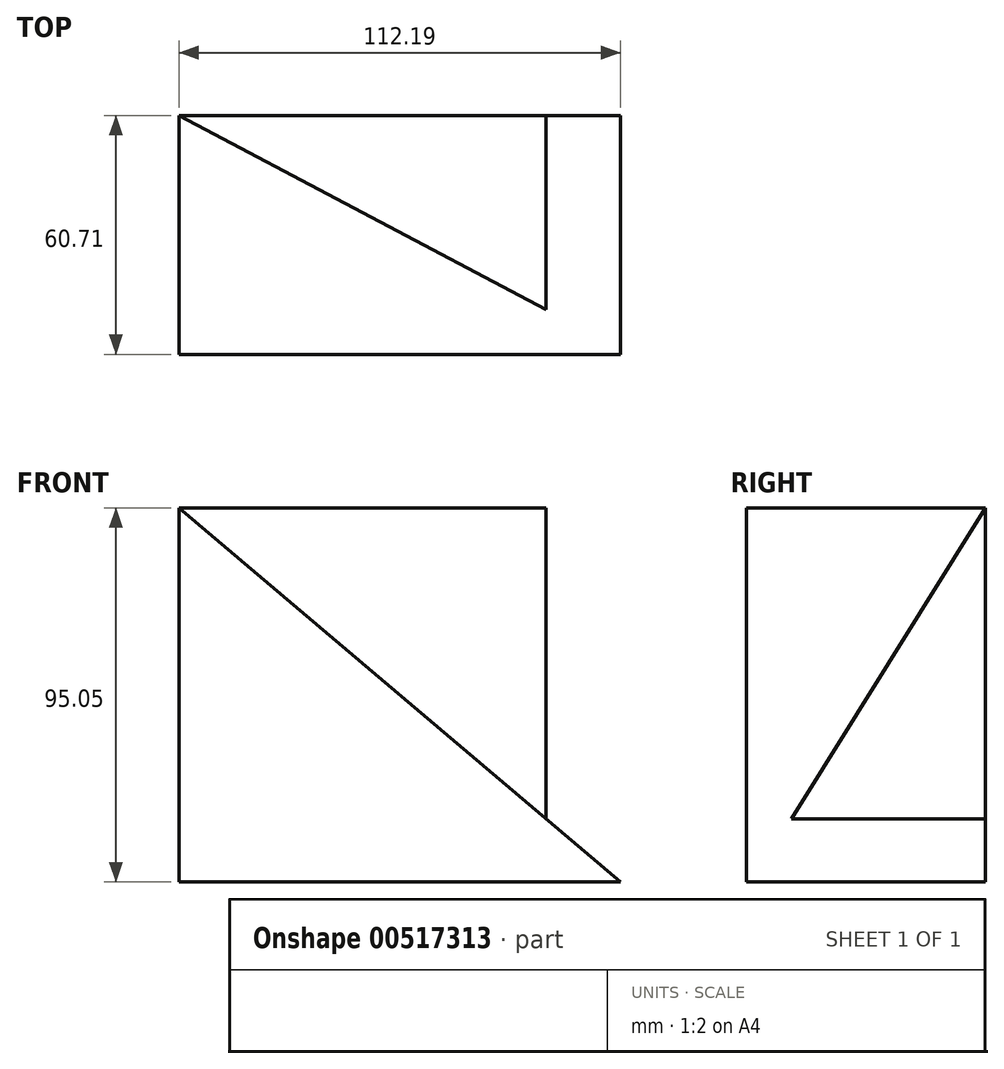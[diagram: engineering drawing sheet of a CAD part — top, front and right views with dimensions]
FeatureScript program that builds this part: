
annotation { "Feature Type Name" : "Feature", "Feature Type Description" : "" }
export const myFeature = defineFeature(function(context is Context, id is Id, definition is map)
    precondition{}
    {
        {
            var Q0;
            Q0=qCreatedBy(makeId("Front.planeOp"),FACE);
            var sketch = newSketch(context, id + "F0", { "sketchPlane" : qUnion([Q0])});
            skLineSegment(sketch, "E0", {"start": v(-65.57, 55.04) * mm, "end": v(-65.57, -40) * mm});
            skLineSegment(sketch, "E1", {"start": v(-65.57, -40) * mm, "end": v(46.62, -40) * mm});
            skLineSegment(sketch, "E2", {"start": v(46.62, -40) * mm, "end": v(-65.57, 55.04) * mm});
            skSolve(sketch);
        }
        {
            var Q0;
            Q0=makeQuery(id+"F0.imprint","IMPRINT",FACE,{"disambiguationData":[TD([[makeQuery(id+"F0.imprint","IMPRINT",EDGE,{"derivedFrom":sQuery(id+"F0.wireOp",EDGE,"E0")}),1.0]])]});
            extrude(context, id + "F1", {"entities" : qUnion([Q0]), "depth" : 60.7 * mm, "offsetDistance" : 25.4 * mm});
        }
        {
            var Q0;
            Q0=makeQuery(id+"F1.opExtrude","SWEPT_FACE",FACE,{"disambiguationData":[OSD([sQuery(id+"F0.wireOp",EDGE,"E0")])]});
            var sketch = newSketch(context, id + "F2", { "sketchPlane" : qUnion([Q0])});
            skLineSegment(sketch, "E3.bottom", {"start": v(0, 55.04) * mm, "end": v(60.7, 55.04) * mm});
            skLineSegment(sketch, "E3.top", {"start": v(0, -40) * mm, "end": v(60.7, -40) * mm});
            skLineSegment(sketch, "E3.left", {"start": v(0, 55.04) * mm, "end": v(0, -40) * mm});
            skLineSegment(sketch, "E3.right", {"start": v(60.7, 55.04) * mm, "end": v(60.7, -40) * mm});
            skLineSegment(sketch, "E4", {"start": v(0, 55.04) * mm, "end": v(60.7, -42.21) * mm});
            skSolve(sketch);
        }
        {
            var Q0;
            {var subQ0=sQuery(id+"F2.wireOp",EDGE,"E3.left");Q0=makeQuery(id+"F2.imprint","IMPRINT",FACE,{"disambiguationData":[TD([[makeQuery(id+"F2.imprint","IMPRINT",EDGE,{"derivedFrom":subQ0}),1.0]])]});}
            extrude(context, id + "F3", {"entities" : qUnion([Q0]), "operationType" : NewBodyOperationType.ADD, "oppositeDirection" : true, "depth" : 93.22 * mm, "offsetDistance" : 25.4 * mm});
        }
    });
